# Revit family: QF_ELECTROLUXPROFESSIONAL_169123_ACPG25
name_source: partatom
category: Specialty Equipment
revit_build: Autodesk Revit 2018 (Build: 20190510_1515(x64)
units: mm (PartAtom-declared; Revit-internal decimal feet)

## family parameters
Always vertical = Yes
Cut with Voids When Loaded = No
Part Type = Normal
Room Calculation Point = No
Round Connector Dimension = Use Diameter
Shared = No
Work Plane-Based = No

## types (1)
- QF_ELECTROLUXPROFESSIONAL_169123_ACPG25
    Cold Water Connection Height = 0"
    Cold Water Maximum Pressure = 0.00 psi
    Cold Water Minimum Pressure = 0.00 psi
    Cold Water Size = 1"
    Description = 1WELL GAS PASTACOOK6, 5GAL/25L 16" - US - AUS
    Direct Waste Size = 1"
    Gas Connection Height = 0"
    Gas Input = 42500.0 Btu/h
    Gas KW = 12.5
    Gas Size = 1"
    HP = 0 HP
    Indirect Waste Connection Height = 0"
    Indirect Waste Size = 2"
    Manufacturer = ELECTROLUX
    Model = 169123
    URL = www.electroluxusa.com/professional
    URL Cutsheet = www.electroluxusa.com/professional
    Watts = 0 W
    Weight in Pounds = 84

## geometry (parser evidence)
native form markers: Sweep x2
no freeform markers — native parametric forms only
